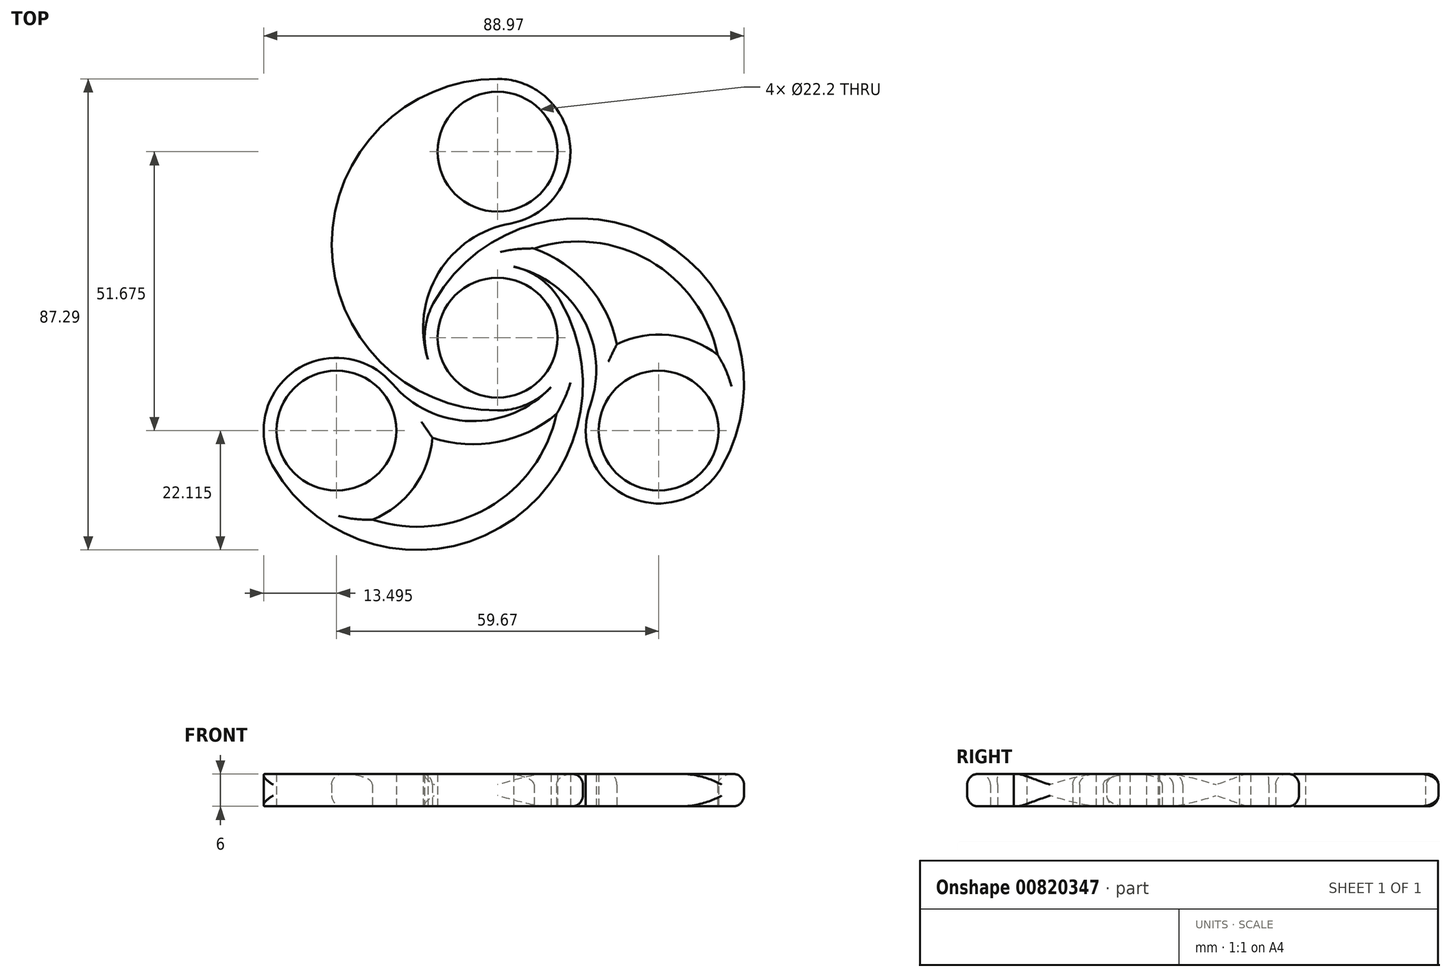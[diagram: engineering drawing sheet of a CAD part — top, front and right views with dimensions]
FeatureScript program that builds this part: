
annotation { "Feature Type Name" : "Feature", "Feature Type Description" : "" }
export const myFeature = defineFeature(function(context is Context, id is Id, definition is map)
    precondition{}
    {
        {
            var Q0;
            Q0=qCreatedBy(makeId("Top.planeOp"),FACE);
            var sketch = newSketch(context, id + "F0", { "sketchPlane" : qUnion([Q0])});
            skCircle(sketch, "E0", {"center": v(0, 34.45) * mm, "radius": 13.5 * mm});
            skCircle(sketch, "E1", {"center": v(0, 0) * mm, "radius": 13.5 * mm});
            skArc(sketch, "E2", {"start": v(0, 47.95) * mm, "mid": v(-30.73, 17.23) * mm, "end": v(0, -13.5) * mm});
            skPoint(sketch, "E3.center", {"position": v(4.82, -6.44) * mm});
            skCircle(sketch, "E4", {"center": v(0, 34.45) * mm, "radius": 11.1 * mm});
            skCircle(sketch, "E5", {"center": v(0, 0) * mm, "radius": 11.1 * mm});
            skArc(sketch, "E6", {"start": v(2.4, 21.16) * mm, "mid": v(-10.91, 12.03) * mm, "end": v(-12.9, -3.99) * mm});
            skCircle(sketch, "E7.1.0", {"center": v(-29.83, -17.23) * mm, "radius": 13.5 * mm});
            skCircle(sketch, "E7.1.1", {"center": v(-29.83, -17.23) * mm, "radius": 11.1 * mm});
            skArc(sketch, "E7.1.2", {"start": v(-41.53, -23.98) * mm, "mid": v(0.45, -35.22) * mm, "end": v(11.7, 6.75) * mm});
            skArc(sketch, "E7.1.3", {"start": v(-19.53, -8.5) * mm, "mid": v(-4.96, -15.47) * mm, "end": v(9.9, -9.17) * mm});
            skCircle(sketch, "E7.2.0", {"center": v(29.83, -17.23) * mm, "radius": 13.5 * mm});
            skCircle(sketch, "E7.2.1", {"center": v(29.83, -17.23) * mm, "radius": 11.1 * mm});
            skArc(sketch, "E7.2.2", {"start": v(41.53, -23.98) * mm, "mid": v(30.28, 18) * mm, "end": v(-11.7, 6.75) * mm});
            skArc(sketch, "E7.2.3", {"start": v(17.13, -12.66) * mm, "mid": v(15.88, 3.44) * mm, "end": v(3, 13.16) * mm});
            skSolve(sketch);
        }
        {
            var Q0;
            Q0=qCreatedBy(makeId("Top.planeOp"),FACE);
            var sketch = newSketch(context, id + "F1", { "sketchPlane" : qUnion([Q0])});
            skArc(sketch, "E8.0.0", {"start": v(0, -13.5) * mm, "mid": v(-8.01, -10.87) * mm, "end": v(-12.9, -3.99) * mm, "construction": true});
            skArc(sketch, "E8.0.1", {"start": v(-12.9, -3.99) * mm, "mid": v(-10.91, 12.03) * mm, "end": v(2.4, 21.16) * mm, "construction": true});
            skArc(sketch, "E8.0.2", {"start": v(2.4, 21.16) * mm, "mid": v(-13.45, 33.25) * mm, "end": v(0, 47.95) * mm, "construction": true});
            skArc(sketch, "E8.0.3", {"start": v(0, 47.95) * mm, "mid": v(-30.73, 17.23) * mm, "end": v(0, -13.5) * mm, "construction": true});
            skArc(sketch, "E9.0", {"start": v(-17.7, -2.4) * mm, "mid": v(-16.75, 9.67) * mm, "end": v(-10.02, 19.74) * mm});
            skArc(sketch, "E9.1", {"start": v(-17.63, 36.91) * mm, "mid": v(-26.43, 17.27) * mm, "end": v(-17.7, -2.4) * mm});
            skArc(sketch, "E9.2", {"start": v(-10.02, 19.74) * mm, "mid": v(-16.27, 27.24) * mm, "end": v(-17.63, 36.91) * mm});
            skArc(sketch, "E10.1.0", {"start": v(-23.15, -33.72) * mm, "mid": v(-1.75, -31.52) * mm, "end": v(10.92, -14.13) * mm});
            skArc(sketch, "E10.1.1", {"start": v(-12.08, -18.55) * mm, "mid": v(-15.45, -27.71) * mm, "end": v(-23.15, -33.72) * mm});
            skArc(sketch, "E10.1.2", {"start": v(10.92, -14.13) * mm, "mid": v(0, -19.34) * mm, "end": v(-12.08, -18.55) * mm});
            skArc(sketch, "E10.2.0", {"start": v(40.78, -3.19) * mm, "mid": v(28.17, 14.25) * mm, "end": v(6.78, 16.53) * mm});
            skArc(sketch, "E10.2.1", {"start": v(22.1, -1.2) * mm, "mid": v(31.73, 0.47) * mm, "end": v(40.78, -3.19) * mm});
            skArc(sketch, "E10.2.2", {"start": v(6.78, 16.53) * mm, "mid": v(16.75, 9.67) * mm, "end": v(22.1, -1.2) * mm});
            skSolve(sketch);
        }
        {
            var Q0;
            Q0=makeQuery(id+"F0.imprint","IMPRINT",FACE,{"disambiguationData":[TD([[makeQuery(id+"F0.imprint","IMPRINT",EDGE,{"derivedFrom":sQuery(id+"F0.wireOp",EDGE,"E4")}),-1.0]])]});
            var Q1;
            Q1=makeQuery(id+"F1.imprint","IMPRINT",FACE,{"disambiguationData":[TD([[makeQuery(id+"F1.imprint","IMPRINT",EDGE,{"derivedFrom":sQuery(id+"F1.wireOp",EDGE,"E8.0.0")}),1.0]])]});
            var Q2;
            {var subQ0=sQuery(id+"F0.wireOp",EDGE,"E7.2.2");Q2=makeQuery(id+"F0.imprint","IMPRINT",FACE,{"disambiguationData":[TD([[makeQuery(id+"F0.imprint","IMPRINT",EDGE,{"derivedFrom":subQ0}),1.0]])]});}
            var Q3;
            {var subQ0=sQuery(id+"F0.wireOp",EDGE,"E7.1.2");Q3=makeQuery(id+"F0.imprint","IMPRINT",FACE,{"disambiguationData":[TD([[makeQuery(id+"F0.imprint","IMPRINT",EDGE,{"derivedFrom":subQ0}),1.0]])]});}
            var Q4;
            Q4=makeQuery(id+"F0.imprint","IMPRINT",FACE,{"disambiguationData":[TD([[makeQuery(id+"F0.imprint","IMPRINT",EDGE,{"derivedFrom":sQuery(id+"F0.wireOp",EDGE,"E5")}),-1.0]])]});
            var Q5;
            Q5=makeQuery(id+"F0.imprint","IMPRINT",FACE,{"disambiguationData":[TD([[makeQuery(id+"F0.imprint","IMPRINT",EDGE,{"derivedFrom":sQuery(id+"F0.wireOp",EDGE,"E7.1.1")}),-1.0]])]});
            var Q6;
            Q6=makeQuery(id+"F0.imprint","IMPRINT",FACE,{"disambiguationData":[TD([[makeQuery(id+"F0.imprint","IMPRINT",EDGE,{"derivedFrom":sQuery(id+"F0.wireOp",EDGE,"E7.2.1")}),-1.0]])]});
            var Q7;
            {var subQ0=sQuery(id+"F0.wireOp",EDGE,"E2");Q7=makeQuery(id+"F0.imprint","IMPRINT",FACE,{"disambiguationData":[TD([[makeQuery(id+"F0.imprint","IMPRINT",EDGE,{"derivedFrom":subQ0}),1.0]])]});}
            extrude(context, id + "F2", {"entities" : qUnion([Q0, Q1, Q2, Q3, Q4, Q5, Q6, Q7]), "depth" : 6 * mm, "offsetDistance" : 25 * mm});
        }
        {
            var Q0;
            Q0=makeQuery(id+"F1.imprint","IMPRINT",FACE,{"disambiguationData":[TD([[makeQuery(id+"F1.imprint","IMPRINT",EDGE,{"derivedFrom":sQuery(id+"F1.wireOp",EDGE,"E9.0")}),1.0]])]});
            var Q1;
            Q1=makeQuery(id+"F1.imprint","IMPRINT",FACE,{"disambiguationData":[TD([[makeQuery(id+"F1.imprint","IMPRINT",EDGE,{"derivedFrom":sQuery(id+"F1.wireOp",EDGE,"E10.2.0")}),1.0]])]});
            var Q2;
            Q2=makeQuery(id+"F1.imprint","IMPRINT",FACE,{"disambiguationData":[TD([[makeQuery(id+"F1.imprint","IMPRINT",EDGE,{"derivedFrom":sQuery(id+"F1.wireOp",EDGE,"E10.1.0")}),1.0]])]});
            extrude(context, id + "F3", {"entities" : qUnion([Q0, Q1, Q2]), "operationType" : NewBodyOperationType.REMOVE, "endBound" : BoundingType.THROUGH_ALL, "depth" : 25 * mm, "offsetDistance" : 25 * mm});
        }
        {
            var Q0;
            Q0=makeQuery(id+"F2.opExtrude","CAP_EDGE",EDGE,{"disambiguationData":[OSD([sQuery(id+"F0.wireOp",EDGE,"E2")])],"isStart":false});
            var Q1;
            Q1=makeQuery(id+"F2.opExtrude","CAP_EDGE",EDGE,{"disambiguationData":[OSD([sQuery(id+"F0.wireOp",EDGE,"E7.1.2")])],"isStart":false});
            var Q2;
            Q2=makeQuery(id+"F2.opExtrude","CAP_EDGE",EDGE,{"disambiguationData":[OSD([sQuery(id+"F0.wireOp",EDGE,"E7.2.2")])],"isStart":false});
            var Q3;
            Q3=makeQuery(id+"F2.opExtrude","CAP_EDGE",EDGE,{"disambiguationData":[OSD([sQuery(id+"F0.wireOp",EDGE,"E7.1.2")])],"isStart":true});
            var Q4;
            Q4=makeQuery(id+"F2.opExtrude","CAP_EDGE",EDGE,{"disambiguationData":[OSD([sQuery(id+"F0.wireOp",EDGE,"E2")])],"isStart":true});
            var Q5;
            Q5=makeQuery(id+"F2.opExtrude","CAP_EDGE",EDGE,{"disambiguationData":[OSD([sQuery(id+"F0.wireOp",EDGE,"E7.2.2")])],"isStart":true});
            var Q6;
            Q6=makeQuery(id+"F3.boolean.opBoolean","INTERSECT",EDGE,{"derivedFrom":[makeQuery(id+"F2.opExtrude","CAP_FACE",FACE,{"disambiguationData":[OSD([sQuery(id+"F0.wireOp",EDGE,"E0"),sQuery(id+"F0.wireOp",EDGE,"E1"),sQuery(id+"F0.wireOp",EDGE,"E2"),sQuery(id+"F0.wireOp",EDGE,"E4"),sQuery(id+"F0.wireOp",EDGE,"E5"),sQuery(id+"F0.wireOp",EDGE,"E6"),sQuery(id+"F0.wireOp",EDGE,"E7.1.0"),sQuery(id+"F0.wireOp",EDGE,"E7.1.1"),sQuery(id+"F0.wireOp",EDGE,"E7.1.2"),sQuery(id+"F0.wireOp",EDGE,"E7.1.3"),sQuery(id+"F0.wireOp",EDGE,"E7.2.0"),sQuery(id+"F0.wireOp",EDGE,"E7.2.1"),sQuery(id+"F0.wireOp",EDGE,"E7.2.2"),sQuery(id+"F0.wireOp",EDGE,"E7.2.3")])],"isStart":false}),makeQuery(id+"F3.opExtrude","SWEPT_FACE",FACE,{"disambiguationData":[OSD([sQuery(id+"F1.wireOp",EDGE,"E10.1.1")])]})]});
            var Q7;
            Q7=makeQuery(id+"F3.boolean.opBoolean","INTERSECT",EDGE,{"derivedFrom":[makeQuery(id+"F2.opExtrude","CAP_FACE",FACE,{"disambiguationData":[OSD([sQuery(id+"F0.wireOp",EDGE,"E0"),sQuery(id+"F0.wireOp",EDGE,"E1"),sQuery(id+"F0.wireOp",EDGE,"E2"),sQuery(id+"F0.wireOp",EDGE,"E4"),sQuery(id+"F0.wireOp",EDGE,"E5"),sQuery(id+"F0.wireOp",EDGE,"E6"),sQuery(id+"F0.wireOp",EDGE,"E7.1.0"),sQuery(id+"F0.wireOp",EDGE,"E7.1.1"),sQuery(id+"F0.wireOp",EDGE,"E7.1.2"),sQuery(id+"F0.wireOp",EDGE,"E7.1.3"),sQuery(id+"F0.wireOp",EDGE,"E7.2.0"),sQuery(id+"F0.wireOp",EDGE,"E7.2.1"),sQuery(id+"F0.wireOp",EDGE,"E7.2.2"),sQuery(id+"F0.wireOp",EDGE,"E7.2.3")])],"isStart":false}),makeQuery(id+"F3.opExtrude","SWEPT_FACE",FACE,{"disambiguationData":[OSD([sQuery(id+"F1.wireOp",EDGE,"E10.1.2")])]})]});
            var Q8;
            Q8=makeQuery(id+"F3.boolean.opBoolean","INTERSECT",EDGE,{"derivedFrom":[makeQuery(id+"F2.opExtrude","CAP_FACE",FACE,{"disambiguationData":[OSD([sQuery(id+"F0.wireOp",EDGE,"E0"),sQuery(id+"F0.wireOp",EDGE,"E1"),sQuery(id+"F0.wireOp",EDGE,"E2"),sQuery(id+"F0.wireOp",EDGE,"E4"),sQuery(id+"F0.wireOp",EDGE,"E5"),sQuery(id+"F0.wireOp",EDGE,"E6"),sQuery(id+"F0.wireOp",EDGE,"E7.1.0"),sQuery(id+"F0.wireOp",EDGE,"E7.1.1"),sQuery(id+"F0.wireOp",EDGE,"E7.1.2"),sQuery(id+"F0.wireOp",EDGE,"E7.1.3"),sQuery(id+"F0.wireOp",EDGE,"E7.2.0"),sQuery(id+"F0.wireOp",EDGE,"E7.2.1"),sQuery(id+"F0.wireOp",EDGE,"E7.2.2"),sQuery(id+"F0.wireOp",EDGE,"E7.2.3")])],"isStart":false}),makeQuery(id+"F3.opExtrude","SWEPT_FACE",FACE,{"disambiguationData":[OSD([sQuery(id+"F1.wireOp",EDGE,"E10.1.0")])]})]});
            var Q9;
            Q9=makeQuery(id+"F3.boolean.opBoolean","INTERSECT",EDGE,{"derivedFrom":[makeQuery(id+"F2.opExtrude","CAP_FACE",FACE,{"disambiguationData":[OSD([sQuery(id+"F0.wireOp",EDGE,"E0"),sQuery(id+"F0.wireOp",EDGE,"E1"),sQuery(id+"F0.wireOp",EDGE,"E2"),sQuery(id+"F0.wireOp",EDGE,"E4"),sQuery(id+"F0.wireOp",EDGE,"E5"),sQuery(id+"F0.wireOp",EDGE,"E6"),sQuery(id+"F0.wireOp",EDGE,"E7.1.0"),sQuery(id+"F0.wireOp",EDGE,"E7.1.1"),sQuery(id+"F0.wireOp",EDGE,"E7.1.2"),sQuery(id+"F0.wireOp",EDGE,"E7.1.3"),sQuery(id+"F0.wireOp",EDGE,"E7.2.0"),sQuery(id+"F0.wireOp",EDGE,"E7.2.1"),sQuery(id+"F0.wireOp",EDGE,"E7.2.2"),sQuery(id+"F0.wireOp",EDGE,"E7.2.3")])],"isStart":false}),makeQuery(id+"F3.opExtrude","SWEPT_FACE",FACE,{"disambiguationData":[OSD([sQuery(id+"F1.wireOp",EDGE,"E10.2.1")])]})]});
            var Q10;
            Q10=makeQuery(id+"F3.boolean.opBoolean","INTERSECT",EDGE,{"derivedFrom":[makeQuery(id+"F2.opExtrude","CAP_FACE",FACE,{"disambiguationData":[OSD([sQuery(id+"F0.wireOp",EDGE,"E0"),sQuery(id+"F0.wireOp",EDGE,"E1"),sQuery(id+"F0.wireOp",EDGE,"E2"),sQuery(id+"F0.wireOp",EDGE,"E4"),sQuery(id+"F0.wireOp",EDGE,"E5"),sQuery(id+"F0.wireOp",EDGE,"E6"),sQuery(id+"F0.wireOp",EDGE,"E7.1.0"),sQuery(id+"F0.wireOp",EDGE,"E7.1.1"),sQuery(id+"F0.wireOp",EDGE,"E7.1.2"),sQuery(id+"F0.wireOp",EDGE,"E7.1.3"),sQuery(id+"F0.wireOp",EDGE,"E7.2.0"),sQuery(id+"F0.wireOp",EDGE,"E7.2.1"),sQuery(id+"F0.wireOp",EDGE,"E7.2.2"),sQuery(id+"F0.wireOp",EDGE,"E7.2.3")])],"isStart":false}),makeQuery(id+"F3.opExtrude","SWEPT_FACE",FACE,{"disambiguationData":[OSD([sQuery(id+"F1.wireOp",EDGE,"E10.2.0")])]})]});
            var Q11;
            Q11=makeQuery(id+"F3.boolean.opBoolean","INTERSECT",EDGE,{"derivedFrom":[makeQuery(id+"F2.opExtrude","CAP_FACE",FACE,{"disambiguationData":[OSD([sQuery(id+"F0.wireOp",EDGE,"E0"),sQuery(id+"F0.wireOp",EDGE,"E1"),sQuery(id+"F0.wireOp",EDGE,"E2"),sQuery(id+"F0.wireOp",EDGE,"E4"),sQuery(id+"F0.wireOp",EDGE,"E5"),sQuery(id+"F0.wireOp",EDGE,"E6"),sQuery(id+"F0.wireOp",EDGE,"E7.1.0"),sQuery(id+"F0.wireOp",EDGE,"E7.1.1"),sQuery(id+"F0.wireOp",EDGE,"E7.1.2"),sQuery(id+"F0.wireOp",EDGE,"E7.1.3"),sQuery(id+"F0.wireOp",EDGE,"E7.2.0"),sQuery(id+"F0.wireOp",EDGE,"E7.2.1"),sQuery(id+"F0.wireOp",EDGE,"E7.2.2"),sQuery(id+"F0.wireOp",EDGE,"E7.2.3")])],"isStart":false}),makeQuery(id+"F3.opExtrude","SWEPT_FACE",FACE,{"disambiguationData":[OSD([sQuery(id+"F1.wireOp",EDGE,"E10.2.2")])]})]});
            var Q12;
            Q12=makeQuery(id+"F3.boolean.opBoolean","INTERSECT",EDGE,{"derivedFrom":[makeQuery(id+"F2.opExtrude","CAP_FACE",FACE,{"disambiguationData":[OSD([sQuery(id+"F0.wireOp",EDGE,"E0"),sQuery(id+"F0.wireOp",EDGE,"E1"),sQuery(id+"F0.wireOp",EDGE,"E2"),sQuery(id+"F0.wireOp",EDGE,"E4"),sQuery(id+"F0.wireOp",EDGE,"E5"),sQuery(id+"F0.wireOp",EDGE,"E6"),sQuery(id+"F0.wireOp",EDGE,"E7.1.0"),sQuery(id+"F0.wireOp",EDGE,"E7.1.1"),sQuery(id+"F0.wireOp",EDGE,"E7.1.2"),sQuery(id+"F0.wireOp",EDGE,"E7.1.3"),sQuery(id+"F0.wireOp",EDGE,"E7.2.0"),sQuery(id+"F0.wireOp",EDGE,"E7.2.1"),sQuery(id+"F0.wireOp",EDGE,"E7.2.2"),sQuery(id+"F0.wireOp",EDGE,"E7.2.3")])],"isStart":false}),makeQuery(id+"F3.opExtrude","SWEPT_FACE",FACE,{"disambiguationData":[OSD([sQuery(id+"F1.wireOp",EDGE,"E9.0")])]})]});
            var Q13;
            Q13=makeQuery(id+"F3.boolean.opBoolean","INTERSECT",EDGE,{"derivedFrom":[makeQuery(id+"F2.opExtrude","CAP_FACE",FACE,{"disambiguationData":[OSD([sQuery(id+"F0.wireOp",EDGE,"E0"),sQuery(id+"F0.wireOp",EDGE,"E1"),sQuery(id+"F0.wireOp",EDGE,"E2"),sQuery(id+"F0.wireOp",EDGE,"E4"),sQuery(id+"F0.wireOp",EDGE,"E5"),sQuery(id+"F0.wireOp",EDGE,"E6"),sQuery(id+"F0.wireOp",EDGE,"E7.1.0"),sQuery(id+"F0.wireOp",EDGE,"E7.1.1"),sQuery(id+"F0.wireOp",EDGE,"E7.1.2"),sQuery(id+"F0.wireOp",EDGE,"E7.1.3"),sQuery(id+"F0.wireOp",EDGE,"E7.2.0"),sQuery(id+"F0.wireOp",EDGE,"E7.2.1"),sQuery(id+"F0.wireOp",EDGE,"E7.2.2"),sQuery(id+"F0.wireOp",EDGE,"E7.2.3")])],"isStart":false}),makeQuery(id+"F3.opExtrude","SWEPT_FACE",FACE,{"disambiguationData":[OSD([sQuery(id+"F1.wireOp",EDGE,"E9.2")])]})]});
            var Q14;
            Q14=makeQuery(id+"F3.boolean.opBoolean","INTERSECT",EDGE,{"derivedFrom":[makeQuery(id+"F2.opExtrude","CAP_FACE",FACE,{"disambiguationData":[OSD([sQuery(id+"F0.wireOp",EDGE,"E0"),sQuery(id+"F0.wireOp",EDGE,"E1"),sQuery(id+"F0.wireOp",EDGE,"E2"),sQuery(id+"F0.wireOp",EDGE,"E4"),sQuery(id+"F0.wireOp",EDGE,"E5"),sQuery(id+"F0.wireOp",EDGE,"E6"),sQuery(id+"F0.wireOp",EDGE,"E7.1.0"),sQuery(id+"F0.wireOp",EDGE,"E7.1.1"),sQuery(id+"F0.wireOp",EDGE,"E7.1.2"),sQuery(id+"F0.wireOp",EDGE,"E7.1.3"),sQuery(id+"F0.wireOp",EDGE,"E7.2.0"),sQuery(id+"F0.wireOp",EDGE,"E7.2.1"),sQuery(id+"F0.wireOp",EDGE,"E7.2.2"),sQuery(id+"F0.wireOp",EDGE,"E7.2.3")])],"isStart":false}),makeQuery(id+"F3.opExtrude","SWEPT_FACE",FACE,{"disambiguationData":[OSD([sQuery(id+"F1.wireOp",EDGE,"E9.1")])]})]});
            var Q15;
            Q15=makeQuery(id+"F3.boolean.opBoolean","COPY",EDGE,{"derivedFrom":makeQuery(id+"F3.opExtrude","CAP_EDGE",EDGE,{"disambiguationData":[OSD([sQuery(id+"F1.wireOp",EDGE,"E9.2")])],"isStart":true})});
            var Q16;
            Q16=makeQuery(id+"F3.boolean.opBoolean","COPY",EDGE,{"derivedFrom":makeQuery(id+"F3.opExtrude","CAP_EDGE",EDGE,{"disambiguationData":[OSD([sQuery(id+"F1.wireOp",EDGE,"E9.1")])],"isStart":true})});
            var Q17;
            Q17=makeQuery(id+"F3.boolean.opBoolean","COPY",EDGE,{"derivedFrom":makeQuery(id+"F3.opExtrude","CAP_EDGE",EDGE,{"disambiguationData":[OSD([sQuery(id+"F1.wireOp",EDGE,"E9.0")])],"isStart":true})});
            var Q18;
            Q18=makeQuery(id+"F3.boolean.opBoolean","COPY",EDGE,{"derivedFrom":makeQuery(id+"F3.opExtrude","CAP_EDGE",EDGE,{"disambiguationData":[OSD([sQuery(id+"F1.wireOp",EDGE,"E10.1.1")])],"isStart":true})});
            var Q19;
            Q19=makeQuery(id+"F3.boolean.opBoolean","COPY",EDGE,{"derivedFrom":makeQuery(id+"F3.opExtrude","CAP_EDGE",EDGE,{"disambiguationData":[OSD([sQuery(id+"F1.wireOp",EDGE,"E10.1.2")])],"isStart":true})});
            var Q20;
            Q20=makeQuery(id+"F3.boolean.opBoolean","COPY",EDGE,{"derivedFrom":makeQuery(id+"F3.opExtrude","CAP_EDGE",EDGE,{"disambiguationData":[OSD([sQuery(id+"F1.wireOp",EDGE,"E10.1.0")])],"isStart":true})});
            var Q21;
            Q21=makeQuery(id+"F3.boolean.opBoolean","COPY",EDGE,{"derivedFrom":makeQuery(id+"F3.opExtrude","CAP_EDGE",EDGE,{"disambiguationData":[OSD([sQuery(id+"F1.wireOp",EDGE,"E10.2.2")])],"isStart":true})});
            var Q22;
            Q22=makeQuery(id+"F3.boolean.opBoolean","COPY",EDGE,{"derivedFrom":makeQuery(id+"F3.opExtrude","CAP_EDGE",EDGE,{"disambiguationData":[OSD([sQuery(id+"F1.wireOp",EDGE,"E10.2.1")])],"isStart":true})});
            var Q23;
            Q23=makeQuery(id+"F3.boolean.opBoolean","COPY",EDGE,{"derivedFrom":makeQuery(id+"F3.opExtrude","CAP_EDGE",EDGE,{"disambiguationData":[OSD([sQuery(id+"F1.wireOp",EDGE,"E10.2.0")])],"isStart":true})});
            fillet(context, id + "F4", {"entities" : qUnion([Q0, Q1, Q2, Q3, Q4, Q5, Q6, Q7, Q8, Q9, Q10, Q11, Q12, Q13, Q14, Q15, Q16, Q17, Q18, Q19, Q20, Q21, Q22, Q23]), "radius" : 2 * mm, "allowEdgeOverflow" : false});
        }
    });
